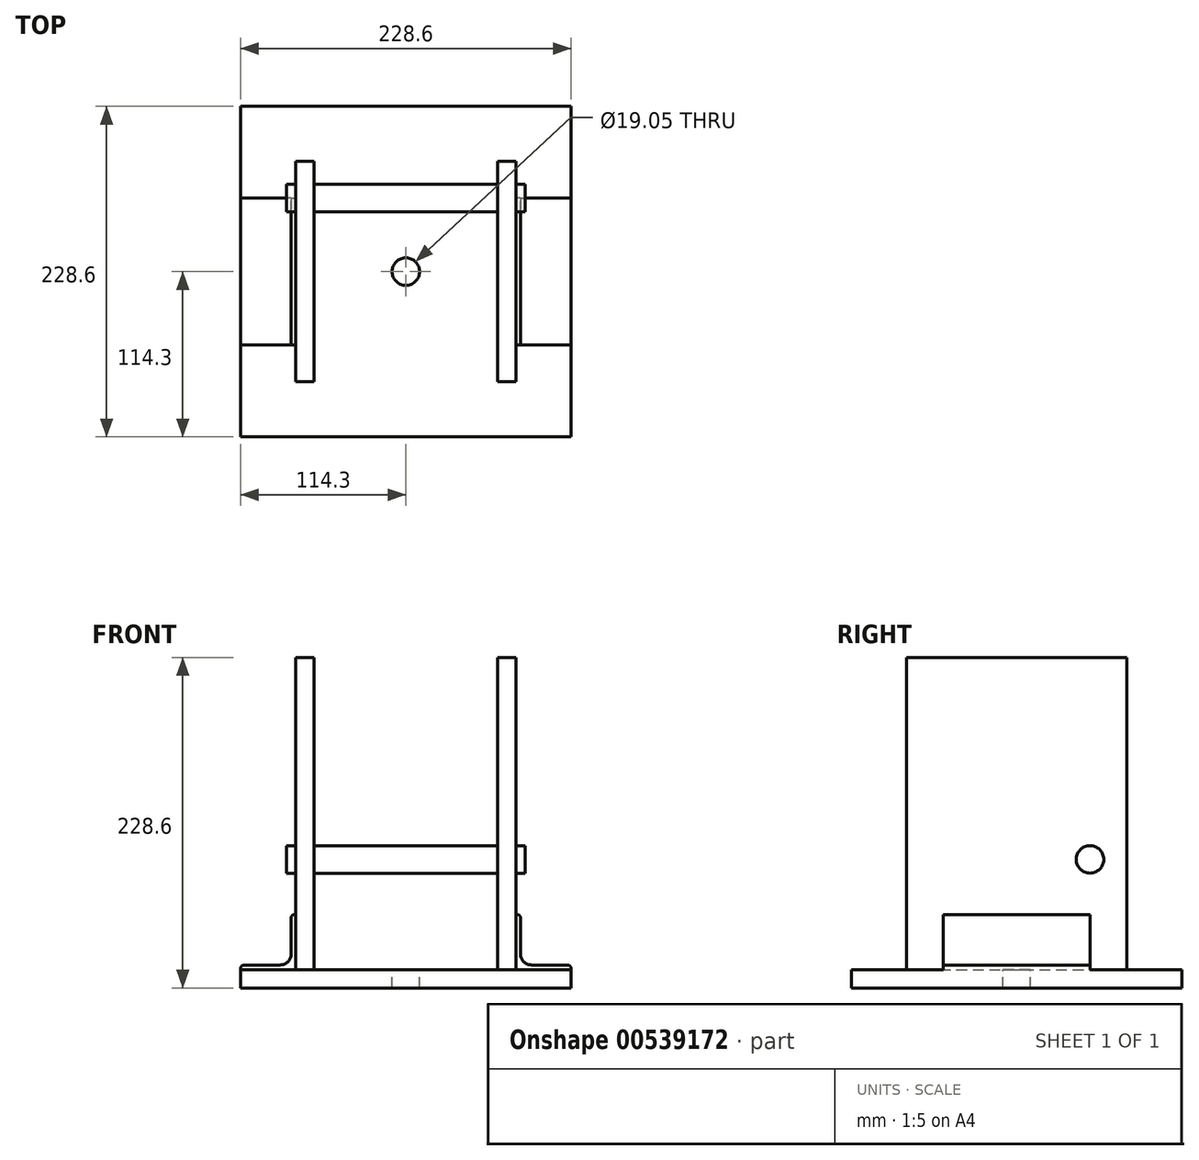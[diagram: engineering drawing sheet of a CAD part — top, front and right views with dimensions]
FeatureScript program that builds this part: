
annotation { "Feature Type Name" : "Feature", "Feature Type Description" : "" }
export const myFeature = defineFeature(function(context is Context, id is Id, definition is map)
    precondition{}
    {
        {
            var Q0;
            Q0=qCreatedBy(makeId("Top.planeOp"),FACE);
            var sketch = newSketch(context, id + "F0", { "sketchPlane" : qUnion([Q0])});
            skLineSegment(sketch, "E0.bottom", {"start": v(114.3, -114.3) * mm, "end": v(-114.3, -114.3) * mm});
            skLineSegment(sketch, "E0.top", {"start": v(114.3, 114.3) * mm, "end": v(-114.3, 114.3) * mm});
            skLineSegment(sketch, "E0.left", {"start": v(114.3, -114.3) * mm, "end": v(114.3, 114.3) * mm});
            skLineSegment(sketch, "E0.right", {"start": v(-114.3, -114.3) * mm, "end": v(-114.3, 114.3) * mm});
            skPoint(sketch, "E0.middle", {"position": v(0, 0) * mm});
            skSolve(sketch);
        }
        {
            var Q0;
            Q0 = qSketchRegion(id + "F0", true);
            extrude(context, id + "F1", {"entities" : qUnion([Q0]), "depth" : 12.7 * mm, "offsetDistance" : 25.4 * mm});
        }
        {
            var Q0;
            Q0=qCreatedBy(makeId("Right.planeOp"),FACE);
            var sketch = newSketch(context, id + "F2", { "sketchPlane" : qUnion([Q0])});
            skLineSegment(sketch, "E1.bottom", {"start": v(-76.2, 228.6) * mm, "end": v(76.2, 228.6) * mm});
            skLineSegment(sketch, "E1.top", {"start": v(-76.2, 12.7) * mm, "end": v(76.2, 12.7) * mm});
            skLineSegment(sketch, "E1.left", {"start": v(-76.2, 228.6) * mm, "end": v(-76.2, 12.7) * mm});
            skLineSegment(sketch, "E1.right", {"start": v(76.2, 228.6) * mm, "end": v(76.2, 12.7) * mm});
            skSolve(sketch);
        }
        {
            var Q0;
            Q0 = qSketchRegion(id + "F2", true);
            extrude(context, id + "F3", {"entities" : qUnion([Q0]), "operationType" : NewBodyOperationType.ADD, "endBound" : BoundingType.SYMMETRIC, "depth" : 152.4 * mm, "offsetDistance" : 25.4 * mm});
        }
        {
            var Q0;
            Q0 = qSketchRegion(id + "F2", true);
            extrude(context, id + "F4", {"entities" : qUnion([Q0]), "operationType" : NewBodyOperationType.REMOVE, "endBound" : BoundingType.SYMMETRIC, "oppositeDirection" : true, "depth" : 127 * mm, "offsetDistance" : 25.4 * mm});
        }
        {
            var Q0;
            Q0=qCreatedBy(makeId("Top.planeOp"),FACE);
            var sketch = newSketch(context, id + "F5", { "sketchPlane" : qUnion([Q0])});
            skCircle(sketch, "E2", {"center": v(0, 0) * mm, "radius": 9.53 * mm});
            skSolve(sketch);
        }
        {
            var Q0;
            Q0 = qSketchRegion(id + "F5", true);
            extrude(context, id + "F6", {"entities" : qUnion([Q0]), "operationType" : NewBodyOperationType.REMOVE, "endBound" : BoundingType.SYMMETRIC, "oppositeDirection" : true, "depth" : 25.4 * mm, "offsetDistance" : 25.4 * mm});
        }
        {
            var Q0;
            Q0=qCreatedBy(makeId("Right.planeOp"),FACE);
            var sketch = newSketch(context, id + "F7", { "sketchPlane" : qUnion([Q0])});
            skCircle(sketch, "E3", {"center": v(50.8, 88.9) * mm, "radius": 9.53 * mm});
            skSolve(sketch);
        }
        {
            var Q0;
            Q0 = qSketchRegion(id + "F7", true);
            extrude(context, id + "F8", {"entities" : qUnion([Q0]), "operationType" : NewBodyOperationType.ADD, "endBound" : BoundingType.SYMMETRIC, "depth" : 165.1 * mm, "offsetDistance" : 25.4 * mm});
        }
        {
            var Q0;
            Q0=qCreatedBy(makeId("Top.planeOp"),FACE);
            var sketch = newSketch(context, id + "F9", { "sketchPlane" : qUnion([Q0])});
            skLineSegment(sketch, "E4.bottom", {"start": v(-114.3, 50.8) * mm, "end": v(-76.2, 50.8) * mm});
            skLineSegment(sketch, "E4.top", {"start": v(-114.3, -50.8) * mm, "end": v(-76.2, -50.8) * mm});
            skLineSegment(sketch, "E4.left", {"start": v(-114.3, 50.8) * mm, "end": v(-114.3, -50.8) * mm});
            skLineSegment(sketch, "E4.right", {"start": v(-76.2, 50.8) * mm, "end": v(-76.2, -50.8) * mm});
            skLineSegment(sketch, "E5.MirrorCS", {"start": v(114.3, 50.8) * mm, "end": v(76.2, 50.8) * mm});
            skLineSegment(sketch, "E6.MirrorCS", {"start": v(76.2, 50.8) * mm, "end": v(76.2, -50.8) * mm});
            skLineSegment(sketch, "E7.MirrorCS", {"start": v(114.3, 50.8) * mm, "end": v(114.3, -50.8) * mm});
            skLineSegment(sketch, "E8.MirrorCS", {"start": v(114.3, -50.8) * mm, "end": v(76.2, -50.8) * mm});
            skSolve(sketch);
        }
        {
            var Q0;
            Q0 = qSketchRegion(id + "F9", true);
            extrude(context, id + "F10", {"entities" : qUnion([Q0]), "operationType" : NewBodyOperationType.ADD, "depth" : 15.88 * mm, "offsetDistance" : 25.4 * mm});
        }
        {
            var Q0;
            Q0=qCreatedBy(makeId("Top.planeOp"),FACE);
            var sketch = newSketch(context, id + "F11", { "sketchPlane" : qUnion([Q0])});
            skLineSegment(sketch, "E9.bottom", {"start": v(-79.38, 50.8) * mm, "end": v(-76.2, 50.8) * mm});
            skLineSegment(sketch, "E9.top", {"start": v(-79.38, -50.8) * mm, "end": v(-76.2, -50.8) * mm});
            skLineSegment(sketch, "E9.left", {"start": v(-79.37, 50.8) * mm, "end": v(-79.37, -50.8) * mm});
            skLineSegment(sketch, "E9.right", {"start": v(-76.2, 50.8) * mm, "end": v(-76.2, -50.8) * mm});
            skLineSegment(sketch, "E10.MirrorCS", {"start": v(79.37, 50.8) * mm, "end": v(79.37, -50.8) * mm});
            skLineSegment(sketch, "E11.MirrorCS", {"start": v(79.38, 50.8) * mm, "end": v(76.2, 50.8) * mm});
            skLineSegment(sketch, "E12.MirrorCS", {"start": v(76.2, 50.8) * mm, "end": v(76.2, -50.8) * mm});
            skLineSegment(sketch, "E13.MirrorCS", {"start": v(79.38, -50.8) * mm, "end": v(76.2, -50.8) * mm});
            skSolve(sketch);
        }
        {
            var Q0;
            Q0 = qSketchRegion(id + "F11", true);
            extrude(context, id + "F12", {"entities" : qUnion([Q0]), "operationType" : NewBodyOperationType.ADD, "depth" : 50.8 * mm, "offsetDistance" : 25.4 * mm});
        }
        {
            var Q0;
            Q0=makeQuery(id+"F10.opExtrude","CAP_EDGE",EDGE,{"disambiguationData":[OSD([sQuery(id+"F9.wireOp",EDGE,"E4.left")])],"isStart":false});
            var Q1;
            Q1=makeQuery(id+"F12.opExtrude","CAP_EDGE",EDGE,{"disambiguationData":[OSD([sQuery(id+"F11.wireOp",EDGE,"E9.left")])],"isStart":false});
            var Q2;
            Q2=makeQuery(id+"F12.opExtrude","CAP_EDGE",EDGE,{"disambiguationData":[OSD([sQuery(id+"F11.wireOp",EDGE,"E10.MirrorCS")])],"isStart":false});
            var Q3;
            Q3=makeQuery(id+"F10.opExtrude","CAP_EDGE",EDGE,{"disambiguationData":[OSD([sQuery(id+"F9.wireOp",EDGE,"E7.MirrorCS")])],"isStart":false});
            fillet(context, id + "F13", {"entities" : qUnion([Q0, Q1, Q2, Q3]), "radius" : 2.54 * mm, "tangentPropagation" : true, "allowEdgeOverflow" : false});
        }
        {
            var Q0;
            Q0=makeQuery(id+"F12.boolean.opBoolean","INTERSECT",EDGE,{"derivedFrom":[makeQuery(id+"F10.opExtrude","CAP_FACE",FACE,{"disambiguationData":[OSD([sQuery(id+"F9.wireOp",EDGE,"E4.bottom"),sQuery(id+"F9.wireOp",EDGE,"E4.top"),sQuery(id+"F9.wireOp",EDGE,"E4.left"),sQuery(id+"F9.wireOp",EDGE,"E4.right")])],"isStart":false}),makeQuery(id+"F12.opExtrude","SWEPT_FACE",FACE,{"disambiguationData":[OSD([sQuery(id+"F11.wireOp",EDGE,"E9.left")])]})]});
            var Q1;
            Q1=makeQuery(id+"F12.boolean.opBoolean","INTERSECT",EDGE,{"derivedFrom":[makeQuery(id+"F10.opExtrude","CAP_FACE",FACE,{"disambiguationData":[OSD([sQuery(id+"F9.wireOp",EDGE,"E5.MirrorCS"),sQuery(id+"F9.wireOp",EDGE,"E6.MirrorCS"),sQuery(id+"F9.wireOp",EDGE,"E7.MirrorCS"),sQuery(id+"F9.wireOp",EDGE,"E8.MirrorCS")])],"isStart":false}),makeQuery(id+"F12.opExtrude","SWEPT_FACE",FACE,{"disambiguationData":[OSD([sQuery(id+"F11.wireOp",EDGE,"E10.MirrorCS")])]})]});
            fillet(context, id + "F14", {"entities" : qUnion([Q0, Q1]), "radius" : 7.62 * mm, "tangentPropagation" : true, "allowEdgeOverflow" : false});
        }
    });
